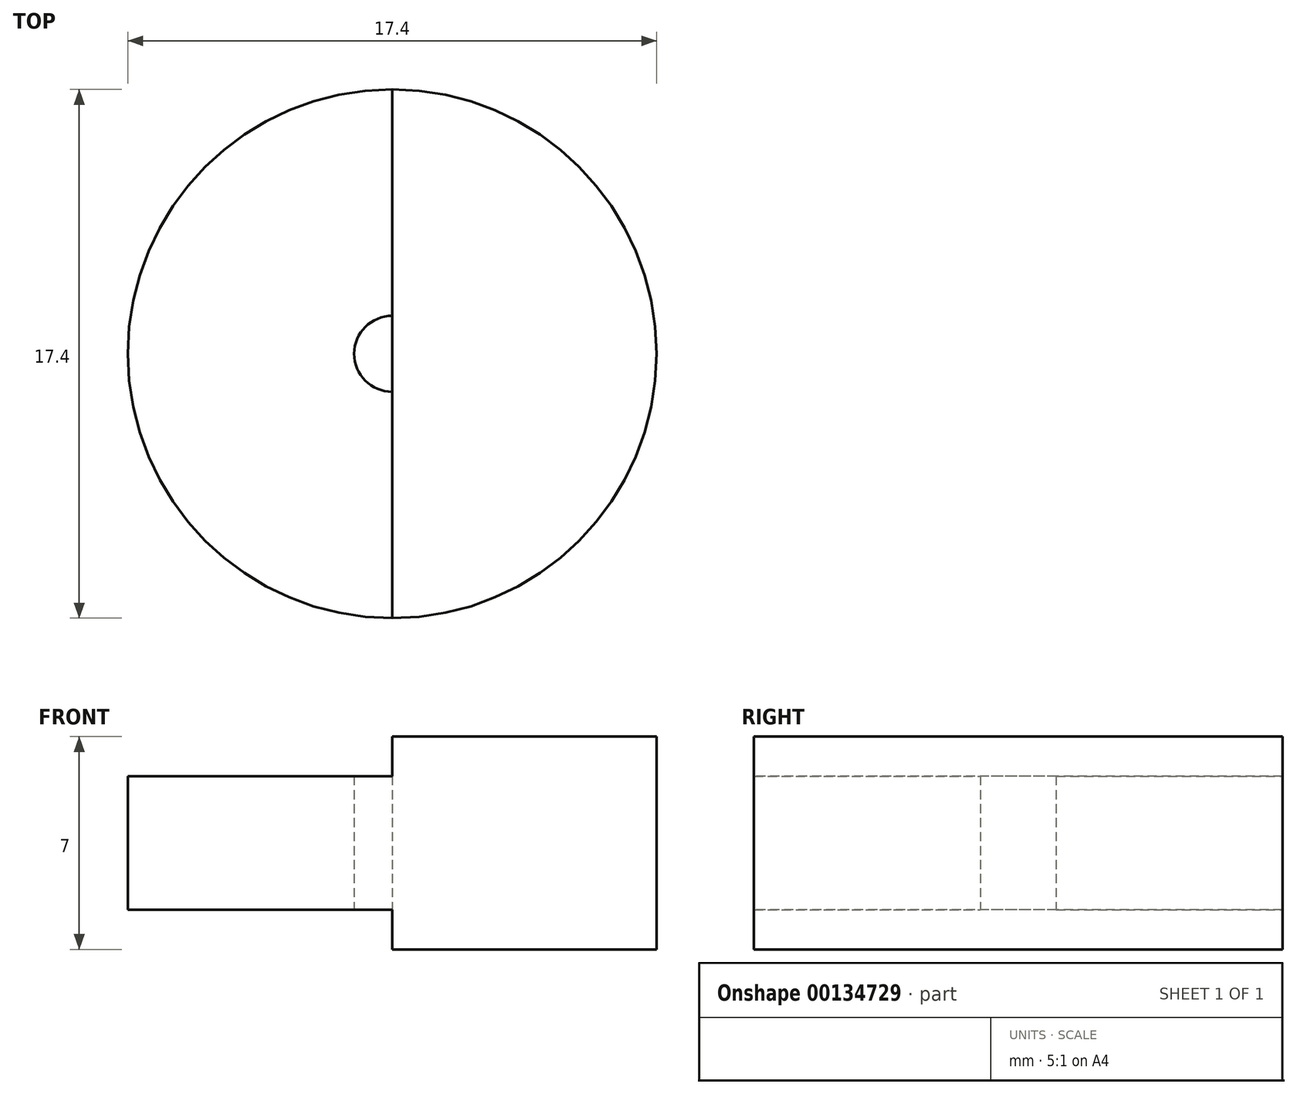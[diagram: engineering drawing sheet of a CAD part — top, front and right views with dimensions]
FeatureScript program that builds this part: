
annotation { "Feature Type Name" : "Feature", "Feature Type Description" : "" }
export const myFeature = defineFeature(function(context is Context, id is Id, definition is map)
    precondition{}
    {
        {
            var Q0;
            Q0=qCreatedBy(makeId("Top.planeOp"),FACE);
            var sketch = newSketch(context, id + "F0", { "sketchPlane" : qUnion([Q0])});
            skCircle(sketch, "E0", {"center": v(-29.23, 0) * mm, "radius": 8.7 * mm});
            skLineSegment(sketch, "E1", {"start": v(-37.93, 0) * mm, "end": v(-20.53, 0) * mm});
            skLineSegment(sketch, "E2", {"start": v(-29.23, 0) * mm, "end": v(-29.23, 8.7) * mm});
            skLineSegment(sketch, "E3", {"start": v(-29.23, 8.7) * mm, "end": v(-29.23, -8.7) * mm});
            skCircle(sketch, "E4", {"center": v(-29.23, 0) * mm, "radius": 1.25 * mm});
            skSolve(sketch);
        }
        {
            var Q0;
            Q0=makeQuery(id+"F0.imprint","IMPRINT",FACE,{"disambiguationData":[TD([[makeQuery(id+"F0.imprint","IMPRINT",EDGE,{"derivedFrom":sQuery(id+"F0.wireOp",EDGE,"E0")}),1.0]])]});
            extrude(context, id + "F1", {"entities" : qUnion([Q0]), "endBound" : BoundingType.SYMMETRIC, "depth" : 4.4 * mm});
        }
        {
            var Q0;
            {var subQ0=sQuery(id+"F0.wireOp",EDGE,"E3");var subQ1=sQuery(id+"F0.wireOp",EDGE,"E1");var subQ2=makeQuery(id+"F0.imprint","INTERSECT",VERTEX,{"derivedFrom":[subQ1,subQ0]});Q0=makeQuery(id+"F0.imprint","IMPRINT",FACE,{"disambiguationData":[TD([[makeQuery(id+"F0.imprint","IMPRINT",EDGE,{"disambiguationData":[TD([[subQ2,-1.0]])],"derivedFrom":subQ1}),-1.0]])]});}
            var Q1;
            {var subQ0=sQuery(id+"F0.wireOp",EDGE,"E3");var subQ1=sQuery(id+"F0.wireOp",EDGE,"E1");var subQ2=makeQuery(id+"F0.imprint","INTERSECT",VERTEX,{"derivedFrom":[subQ1,subQ0]});Q1=makeQuery(id+"F0.imprint","IMPRINT",FACE,{"disambiguationData":[TD([[makeQuery(id+"F0.imprint","IMPRINT",EDGE,{"disambiguationData":[TD([[subQ2,-1.0]])],"derivedFrom":subQ1}),1.0]])]});}
            var Q2;
            {var subQ0=sQuery(id+"F0.wireOp",EDGE,"E4");var subQ1=sQuery(id+"F0.wireOp",EDGE,"E1");var subQ2=makeQuery(id+"F0.imprint","INTERSECT",VERTEX,{"disambiguationData":[OD(0.0)],"derivedFrom":[subQ1,subQ0]});Q2=makeQuery(id+"F0.imprint","IMPRINT",FACE,{"disambiguationData":[TD([[makeQuery(id+"F0.imprint","IMPRINT",EDGE,{"disambiguationData":[TD([[subQ2,-1.0]])],"derivedFrom":subQ1}),1.0]])]});}
            var Q3;
            {var subQ0=sQuery(id+"F0.wireOp",EDGE,"E4");var subQ1=sQuery(id+"F0.wireOp",EDGE,"E1");var subQ2=makeQuery(id+"F0.imprint","INTERSECT",VERTEX,{"disambiguationData":[OD(0.0)],"derivedFrom":[subQ1,subQ0]});Q3=makeQuery(id+"F0.imprint","IMPRINT",FACE,{"disambiguationData":[TD([[makeQuery(id+"F0.imprint","IMPRINT",EDGE,{"disambiguationData":[TD([[subQ2,-1.0]])],"derivedFrom":subQ1}),-1.0]])]});}
            extrude(context, id + "F2", {"entities" : qUnion([Q0, Q1, Q2, Q3]), "operationType" : NewBodyOperationType.ADD, "endBound" : BoundingType.SYMMETRIC, "depth" : 7 * mm});
        }
    });
